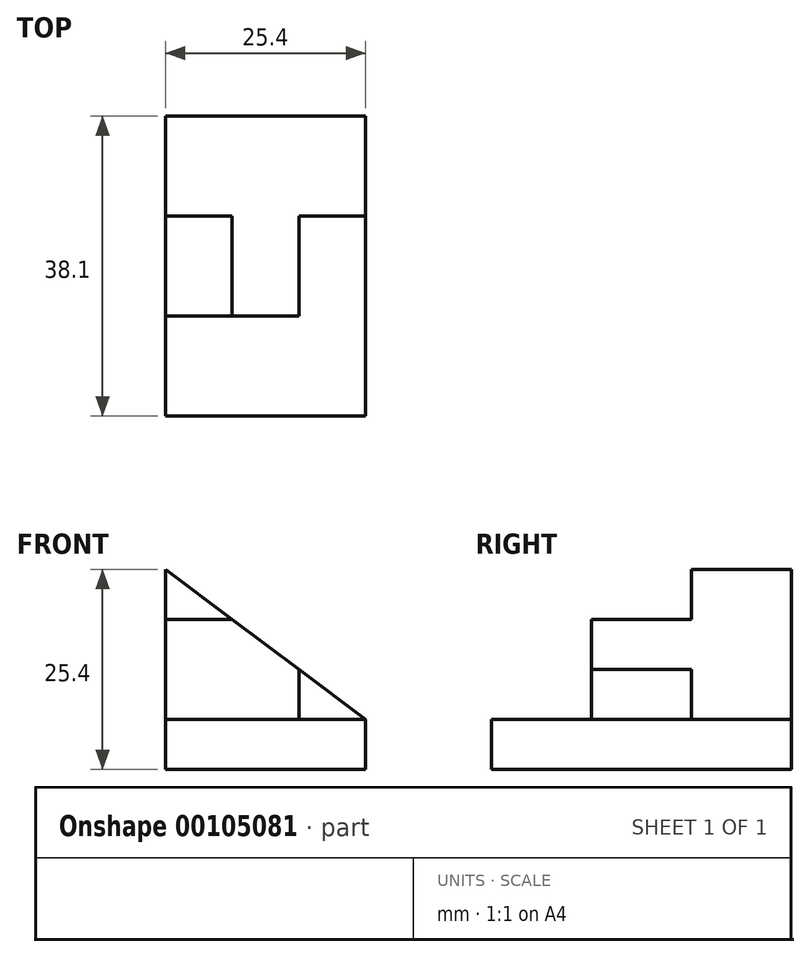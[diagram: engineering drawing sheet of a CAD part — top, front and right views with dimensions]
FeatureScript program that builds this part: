
annotation { "Feature Type Name" : "Feature", "Feature Type Description" : "" }
export const myFeature = defineFeature(function(context is Context, id is Id, definition is map)
    precondition{}
    {
        {
            var Q0;
            Q0=qCreatedBy(makeId("Front.planeOp"),FACE);
            var sketch = newSketch(context, id + "F0", { "sketchPlane" : qUnion([Q0])});
            skLineSegment(sketch, "E0.bottom", {"start": v(0, 0) * mm, "end": v(25.4, 0) * mm});
            skLineSegment(sketch, "E0.top", {"start": v(0, 6.35) * mm, "end": v(25.4, 6.35) * mm});
            skLineSegment(sketch, "E0.left", {"start": v(0, 0) * mm, "end": v(0, 6.35) * mm});
            skLineSegment(sketch, "E0.right", {"start": v(25.4, 0) * mm, "end": v(25.4, 6.35) * mm});
            skLineSegment(sketch, "E1", {"start": v(0, 6.35) * mm, "end": v(0, 25.4) * mm});
            skLineSegment(sketch, "E2", {"start": v(0, 25.4) * mm, "end": v(25.4, 6.35) * mm});
            skSolve(sketch);
        }
        {
            var Q0;
            Q0=makeQuery(id+"F0.imprint","IMPRINT",FACE,{"disambiguationData":[TD([[makeQuery(id+"F0.imprint","IMPRINT",EDGE,{"derivedFrom":sQuery(id+"F0.wireOp",EDGE,"E0.top")}),1.0]])]});
            var Q1;
            Q1=makeQuery(id+"F0.imprint","IMPRINT",FACE,{"disambiguationData":[TD([[makeQuery(id+"F0.imprint","IMPRINT",EDGE,{"derivedFrom":sQuery(id+"F0.wireOp",EDGE,"E0.bottom")}),1.0]])]});
            extrude(context, id + "F1", {"entities" : qUnion([Q0, Q1]), "depth" : 38.1 * mm});
        }
        {
            var Q0;
            Q0=makeQuery(id+"F1.opExtrude","CAP_FACE",FACE,{"disambiguationData":[OSD([sQuery(id+"F0.wireOp",EDGE,"E0.bottom"),sQuery(id+"F0.wireOp",EDGE,"E0.left"),sQuery(id+"F0.wireOp",EDGE,"E0.right"),sQuery(id+"F0.wireOp",EDGE,"E1"),sQuery(id+"F0.wireOp",EDGE,"E2")])],"isStart":false});
            var sketch = newSketch(context, id + "F2", { "sketchPlane" : qUnion([Q0])});
            skLineSegment(sketch, "E3", {"start": v(0, 6.35) * mm, "end": v(0, 25.4) * mm});
            skLineSegment(sketch, "E4", {"start": v(0, 25.4) * mm, "end": v(25.4, 6.35) * mm});
            skLineSegment(sketch, "E5", {"start": v(25.4, 6.35) * mm, "end": v(0, 6.35) * mm});
            skSolve(sketch);
        }
        {
            var Q0;
            Q0 = qSketchRegion(id + "F2", true);
            extrude(context, id + "F3", {"entities" : qUnion([Q0]), "operationType" : NewBodyOperationType.REMOVE, "oppositeDirection" : true, "depth" : 12.7 * mm});
        }
        {
            var Q0;
            Q0=makeQuery(id+"F3.boolean.opBoolean","COPY",FACE,{"derivedFrom":makeQuery(id+"F3.opExtrude","CAP_FACE",FACE,{"disambiguationData":[OSD([sQuery(id+"F2.wireOp",EDGE,"E3"),sQuery(id+"F2.wireOp",EDGE,"E4"),sQuery(id+"F2.wireOp",EDGE,"E5")])],"isStart":false})});
            var sketch = newSketch(context, id + "F4", { "sketchPlane" : qUnion([Q0])});
            skLineSegment(sketch, "E6", {"start": v(0, 25.4) * mm, "end": v(0, 19.05) * mm});
            skLineSegment(sketch, "E7", {"start": v(0, 19.05) * mm, "end": v(8.47, 19.05) * mm});
            skLineSegment(sketch, "E8", {"start": v(8.47, 19.05) * mm, "end": v(0, 25.4) * mm});
            skLineSegment(sketch, "E9", {"start": v(16.93, 12.7) * mm, "end": v(16.93, 6.35) * mm});
            skLineSegment(sketch, "E10", {"start": v(16.93, 6.35) * mm, "end": v(25.4, 6.35) * mm});
            skLineSegment(sketch, "E11", {"start": v(25.4, 6.35) * mm, "end": v(16.93, 12.7) * mm});
            skSolve(sketch);
        }
        {
            var Q0;
            Q0 = qSketchRegion(id + "F4", true);
            extrude(context, id + "F5", {"entities" : qUnion([Q0]), "operationType" : NewBodyOperationType.REMOVE, "oppositeDirection" : true, "depth" : 12.7 * mm});
        }
    });
